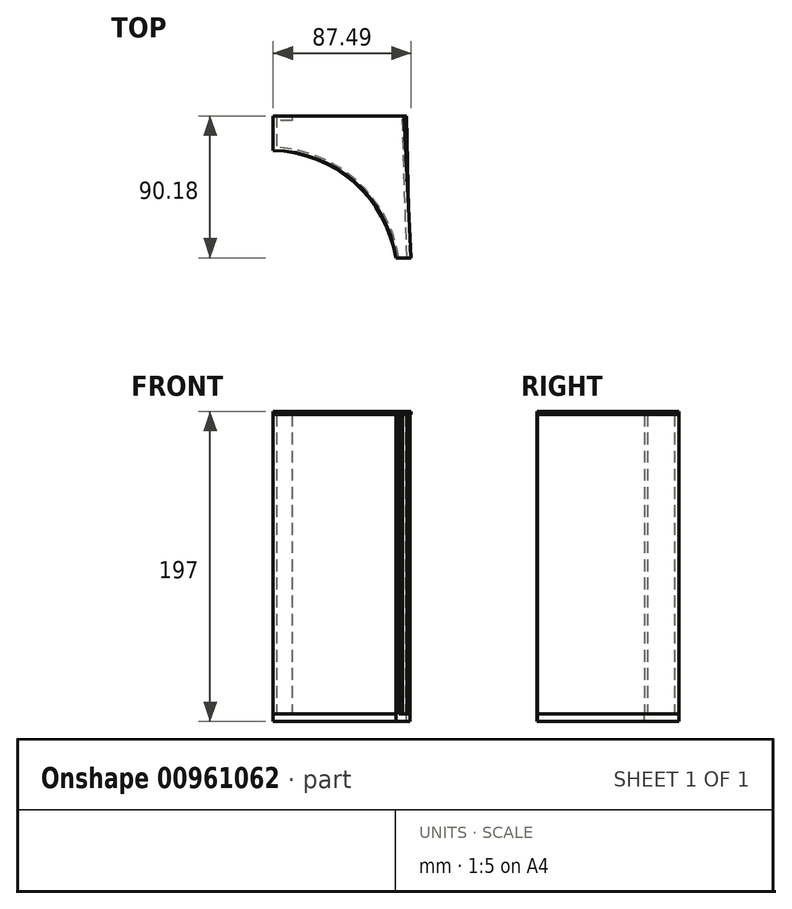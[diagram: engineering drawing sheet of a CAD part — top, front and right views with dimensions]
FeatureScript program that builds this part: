
annotation { "Feature Type Name" : "Feature", "Feature Type Description" : "" }
export const myFeature = defineFeature(function(context is Context, id is Id, definition is map)
    precondition{}
    {
        {
            var Q0;
            Q0=qCreatedBy(makeId("Top.planeOp"),FACE);
            var sketch = newSketch(context, id + "F0", { "sketchPlane" : qUnion([Q0])});
            skLineSegment(sketch, "E0", {"start": v(41.96, -60.76) * mm, "end": v(39.11, 29.2) * mm});
            skLineSegment(sketch, "E1", {"start": v(39.11, 29.2) * mm, "end": v(-40.89, 29.2) * mm});
            skLineSegment(sketch, "E2", {"start": v(41.96, -60.76) * mm, "end": v(36.96, -60.92) * mm});
            skLineSegment(sketch, "E3", {"start": v(-40.89, 29.2) * mm, "end": v(-40.89, 9.2) * mm});
            skArc(sketch, "E4", {"start": v(36.96, -60.92) * mm, "mid": v(10.38, -12.16) * mm, "end": v(-40.89, 9.2) * mm});
            skLineSegment(sketch, "E5", {"start": v(41.96, -60.76) * mm, "end": v(43.96, -60.7) * mm});
            skLineSegment(sketch, "E6", {"start": v(43.96, -60.7) * mm, "end": v(41.11, 29.2) * mm});
            skLineSegment(sketch, "E7", {"start": v(41.11, 29.2) * mm, "end": v(39.11, 29.2) * mm});
            skLineSegment(sketch, "E8", {"start": v(-40.89, 29.2) * mm, "end": v(-42.89, 29.2) * mm});
            skLineSegment(sketch, "E9", {"start": v(-42.89, 29.2) * mm, "end": v(-42.89, 9.62) * mm});
            skLineSegment(sketch, "E10", {"start": v(-40.89, 9.2) * mm, "end": v(-42.89, 9.31) * mm});
            skLineSegment(sketch, "E11", {"start": v(-42.89, 9.31) * mm, "end": v(-42.89, 9.62) * mm});
            skLineSegment(sketch, "E12", {"start": v(-42.89, 9.31) * mm, "end": v(-42.89, 7.31) * mm});
            skLineSegment(sketch, "E13", {"start": v(36.96, -60.92) * mm, "end": v(34.96, -60.98) * mm});
            skArc(sketch, "E14", {"start": v(34.96, -60.98) * mm, "mid": v(8.35, -12.8) * mm, "end": v(-42.89, 7.31) * mm});
            skSolve(sketch);
        }
        {
            var Q0;
            Q0=makeQuery(id+"F0.imprint","IMPRINT",FACE,{"disambiguationData":[TD([[makeQuery(id+"F0.imprint","IMPRINT",EDGE,{"derivedFrom":sQuery(id+"F0.wireOp",EDGE,"E0")}),-1.0]])]});
            var Q1;
            Q1=makeQuery(id+"F0.imprint","IMPRINT",FACE,{"disambiguationData":[TD([[makeQuery(id+"F0.imprint","IMPRINT",EDGE,{"derivedFrom":sQuery(id+"F0.wireOp",EDGE,"E3")}),-1.0]])]});
            var Q2;
            Q2=makeQuery(id+"F0.imprint","IMPRINT",FACE,{"disambiguationData":[TD([[makeQuery(id+"F0.imprint","IMPRINT",EDGE,{"derivedFrom":sQuery(id+"F0.wireOp",EDGE,"E4")}),1.0]])]});
            extrude(context, id + "F1", {"entities" : qUnion([Q0, Q1, Q2]), "depth" : 190 * mm, "offsetDistance" : 25 * mm});
        }
        {
            var Q0;
            Q0=makeQuery(id+"F1.opExtrude","CAP_FACE",FACE,{"disambiguationData":[OSD([sQuery(id+"F0.wireOp",EDGE,"E3"),sQuery(id+"F0.wireOp",EDGE,"E4"),sQuery(id+"F0.wireOp",EDGE,"E8"),sQuery(id+"F0.wireOp",EDGE,"E9"),sQuery(id+"F0.wireOp",EDGE,"E11"),sQuery(id+"F0.wireOp",EDGE,"E12"),sQuery(id+"F0.wireOp",EDGE,"E13"),sQuery(id+"F0.wireOp",EDGE,"E14")])],"isStart":false});
            var sketch = newSketch(context, id + "F2", { "sketchPlane" : qUnion([Q0])});
            skLineSegment(sketch, "E15", {"start": v(-42.89, 29.2) * mm, "end": v(40.27, 29.2) * mm});
            skLineSegment(sketch, "E16", {"start": v(40.27, 29.2) * mm, "end": v(44.6, -60.92) * mm});
            skLineSegment(sketch, "E17", {"start": v(44.6, -60.92) * mm, "end": v(34.96, -60.98) * mm});
            skLineSegment(sketch, "E18", {"start": v(-42.89, 29.2) * mm, "end": v(-42.89, 7.31) * mm});
            skArc(sketch, "E19", {"start": v(34.96, -60.98) * mm, "mid": v(8.68, -12.43) * mm, "end": v(-42.89, 7.31) * mm});
            skSolve(sketch);
        }
        {
            var Q0;
            {var subQ0=sQuery(id+"F2.wireOp",EDGE,"E18");Q0=makeQuery(id+"F2.imprint","IMPRINT",FACE,{"disambiguationData":[TD([[makeQuery(id+"F2.imprint","IMPRINT",EDGE,{"derivedFrom":subQ0}),1.0]])]});}
            var Q1;
            {var subQ1=sQuery(id+"F2.wireOp",EDGE,"E16");Q1=makeQuery(id+"F2.imprint","IMPRINT",FACE,{"disambiguationData":[TD([[makeQuery(id+"F2.imprint","IMPRINT",EDGE,{"derivedFrom":subQ1}),-1.0]])]});}
            extrude(context, id + "F3", {"entities" : qUnion([Q0, Q1]), "depth" : 2 * mm, "offsetDistance" : 25 * mm});
        }
        {
            var Q0;
            Q0=makeQuery(id+"F1.opExtrude","CAP_FACE",FACE,{"disambiguationData":[OSD([sQuery(id+"F0.wireOp",EDGE,"E3"),sQuery(id+"F0.wireOp",EDGE,"E4"),sQuery(id+"F0.wireOp",EDGE,"E8"),sQuery(id+"F0.wireOp",EDGE,"E9"),sQuery(id+"F0.wireOp",EDGE,"E11"),sQuery(id+"F0.wireOp",EDGE,"E12"),sQuery(id+"F0.wireOp",EDGE,"E13"),sQuery(id+"F0.wireOp",EDGE,"E14")])],"isStart":true});
            var sketch = newSketch(context, id + "F4", { "sketchPlane" : qUnion([Q0])});
            skLineSegment(sketch, "E20", {"start": v(-42.89, -29.2) * mm, "end": v(41.7, -29.2) * mm});
            skLineSegment(sketch, "E21", {"start": v(41.7, -29.2) * mm, "end": v(43.86, 60.69) * mm});
            skLineSegment(sketch, "E22", {"start": v(43.86, 60.69) * mm, "end": v(34.96, 60.98) * mm});
            skLineSegment(sketch, "E23", {"start": v(-42.89, -29.2) * mm, "end": v(-42.89, -7.31) * mm});
            skArc(sketch, "E24", {"start": v(-42.89, -7.31) * mm, "mid": v(8.3, 12.87) * mm, "end": v(34.96, 60.98) * mm});
            skSolve(sketch);
        }
        {
            var Q0;
            Q0=makeQuery(id+"F4.imprint","IMPRINT",FACE,{"disambiguationData":[TD([[makeQuery(id+"F4.imprint","IMPRINT",EDGE,{"derivedFrom":sQuery(id+"F4.wireOp",EDGE,"E24")}),-1.0]])]});
            var Q1;
            {var subQ1=sQuery(id+"F4.wireOp",EDGE,"E23");Q1=makeQuery(id+"F4.imprint","IMPRINT",FACE,{"disambiguationData":[TD([[makeQuery(id+"F4.imprint","IMPRINT",EDGE,{"derivedFrom":subQ1}),-1.0]])]});}
            var Q2;
            {var subQ1=sQuery(id+"F4.wireOp",EDGE,"E21");Q2=makeQuery(id+"F4.imprint","IMPRINT",FACE,{"disambiguationData":[TD([[makeQuery(id+"F4.imprint","IMPRINT",EDGE,{"derivedFrom":subQ1}),1.0]])]});}
            extrude(context, id + "F5", {"entities" : qUnion([Q0, Q1, Q2]), "operationType" : NewBodyOperationType.ADD, "depth" : 5 * mm, "offsetDistance" : 25 * mm});
        }
        {
            var Q0;
            Q0=makeQuery(id+"F1.opExtrude","SWEPT_FACE",FACE,{"disambiguationData":[OSD([sQuery(id+"F0.wireOp",EDGE,"E3")])]});
            var sketch = newSketch(context, id + "F6", { "sketchPlane" : qUnion([Q0])});
            skLineSegment(sketch, "E25", {"start": v(29.2, 190) * mm, "end": v(26.2, 190) * mm});
            skLineSegment(sketch, "E26", {"start": v(26.2, 190) * mm, "end": v(26.2, 0) * mm});
            skLineSegment(sketch, "E27", {"start": v(26.2, 0) * mm, "end": v(29.2, 0) * mm});
            skLineSegment(sketch, "E28", {"start": v(29.2, 0) * mm, "end": v(29.2, 190) * mm});
            skSolve(sketch);
        }
        {
            var Q0;
            Q0=makeQuery(id+"F6.imprint","IMPRINT",FACE,{"disambiguationData":[TD([[makeQuery(id+"F6.imprint","IMPRINT",EDGE,{"derivedFrom":sQuery(id+"F6.wireOp",EDGE,"E26")}),1.0]])]});
            extrude(context, id + "F7", {"entities" : qUnion([Q0]), "depth" : 10 * mm, "offsetDistance" : 25 * mm});
        }
    });
